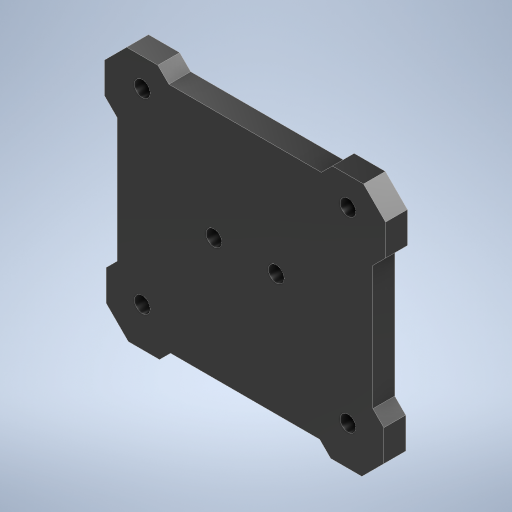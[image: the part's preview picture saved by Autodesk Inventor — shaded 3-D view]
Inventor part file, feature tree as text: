
AUTODESK INVENTOR PART (.ipt)
format: ipt  version: 2024.2 (Build 282272000, 272)  size: 292,352 bytes
history: native  units: in
note: dims shown in document units (in); Inventor stores cm internally (conversion verified against a paired STEP export)
features: other x1, extrude x1, sketch x1
ambient origin geometry x8: Origin, YZ Plane, XZ Plane, XY Plane, X Axis, Y Axis, Z Axis, Center Point
bodies: Solid1 (feature_tree)
feature tree (3):
  other  "Cortar-Extruir-Lámina1"
  extrude  "Extrusion1"  Depth=0.3937in
  sketch  "Sketch1"  dims[d0=0.3937in d1=0.1969in d2=0.3937in d3=0.0in]
